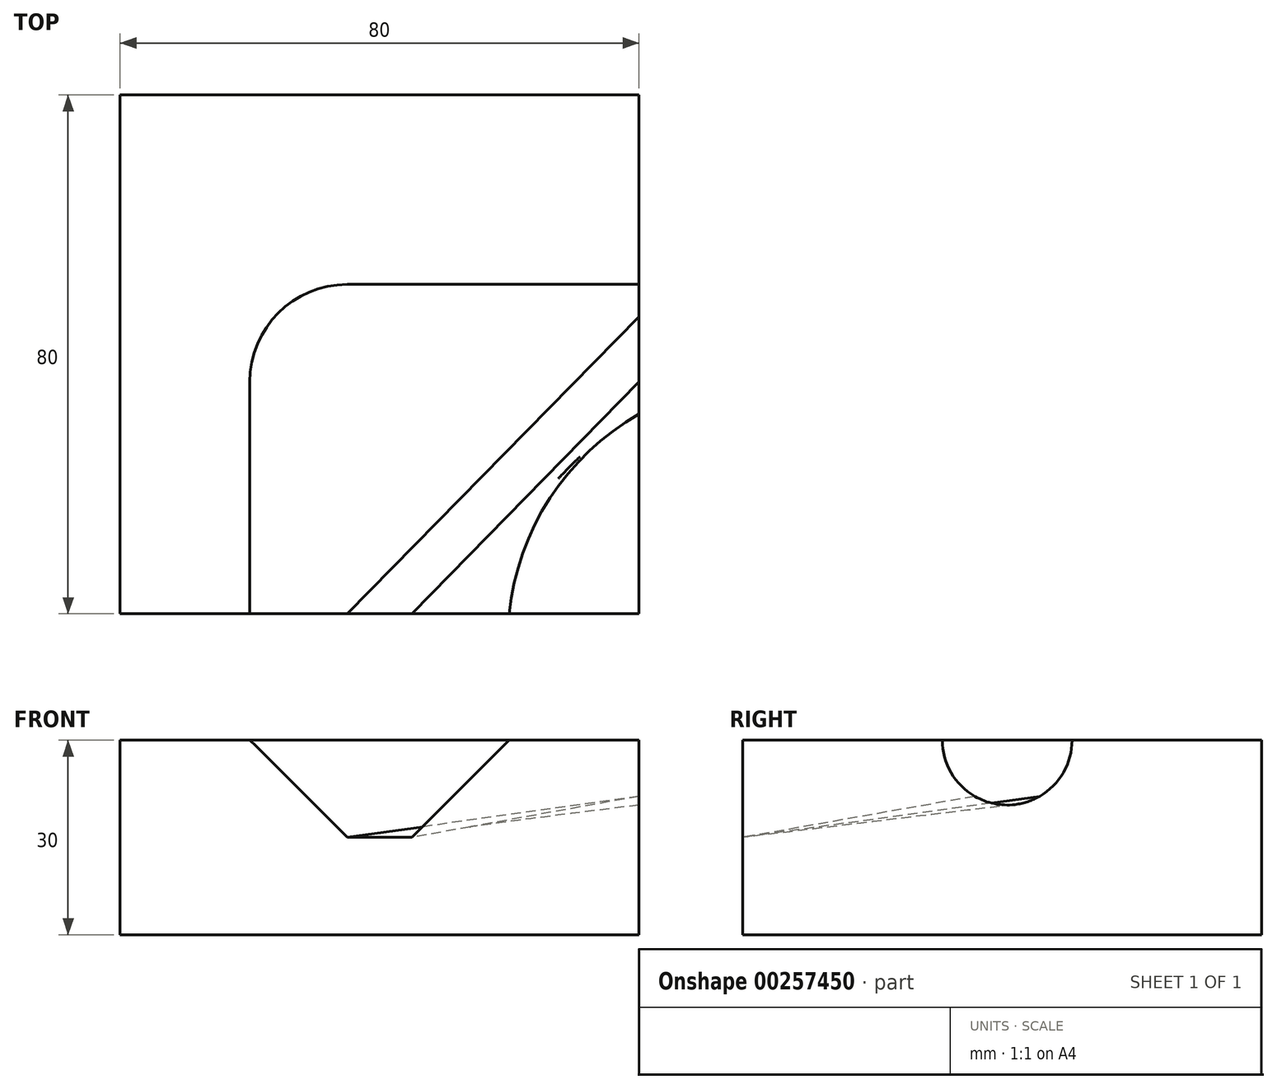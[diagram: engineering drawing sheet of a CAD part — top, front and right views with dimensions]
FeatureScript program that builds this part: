
annotation { "Feature Type Name" : "Feature", "Feature Type Description" : "" }
export const myFeature = defineFeature(function(context is Context, id is Id, definition is map)
    precondition{}
    {
        {
            var Q0;
            Q0=qCreatedBy(makeId("Top.planeOp"),FACE);
            var sketch = newSketch(context, id + "F0", { "sketchPlane" : qUnion([Q0])});
            skLineSegment(sketch, "E0.bottom", {"start": v(-80, 80) * mm, "end": v(0, 80) * mm});
            skLineSegment(sketch, "E0.top", {"start": v(-80, 0) * mm, "end": v(0, 0) * mm});
            skLineSegment(sketch, "E0.left", {"start": v(-80, 80) * mm, "end": v(-80, 0) * mm});
            skLineSegment(sketch, "E0.right", {"start": v(0, 80) * mm, "end": v(0, 0) * mm});
            skArc(sketch, "E1", {"start": v(-45, 50.78) * mm, "mid": v(-55.6, 46.38) * mm, "end": v(-60, 35.78) * mm});
            skArc(sketch, "E2", {"start": v(0, 30.78) * mm, "mid": v(-13.74, 17.82) * mm, "end": v(-20, 0) * mm});
            skLineSegment(sketch, "E3", {"start": v(-45, 50.78) * mm, "end": v(0, 50.78) * mm});
            skLineSegment(sketch, "E4", {"start": v(-60, 35.78) * mm, "end": v(-60, 0) * mm});
            skSolve(sketch);
        }
        {
            var Q0;
            {var subQ1=sQuery(id+"F0.wireOp",EDGE,"E0.bottom");Q0=makeQuery(id+"F0.imprint","IMPRINT",FACE,{"disambiguationData":[TD([[makeQuery(id+"F0.imprint","IMPRINT",EDGE,{"derivedFrom":subQ1}),-1.0]])]});}
            var Q1;
            Q1=makeQuery(id+"F0.imprint","IMPRINT",FACE,{"disambiguationData":[TD([[makeQuery(id+"F0.imprint","IMPRINT",EDGE,{"derivedFrom":sQuery(id+"F0.wireOp",EDGE,"E1")}),1.0]])]});
            var Q2;
            {var subQ3=sQuery(id+"F0.wireOp",EDGE,"E2");Q2=makeQuery(id+"F0.imprint","IMPRINT",FACE,{"disambiguationData":[TD([[makeQuery(id+"F0.imprint","IMPRINT",EDGE,{"derivedFrom":subQ3}),1.0]])]});}
            extrude(context, id + "F1", {"entities" : qUnion([Q0, Q1, Q2]), "oppositeDirection" : true, "depth" : 30 * mm});
        }
        {
            var Q0;
            Q0=makeQuery(id+"F1.opExtrude","SWEPT_FACE",FACE,{"disambiguationData":[OSD([sQuery(id+"F0.wireOp",EDGE,"E0.right")])]});
            cPlane(context, id + "F2", {"entities" : qUnion([Q0]), "cplaneType" : CPlaneType.OFFSET, "offset" : 0 * mm, "width" : 150 * mm, "height" : 150 * mm});
        }
        {
            var Q0;
            Q0=qCreatedBy(id+"F2.planeOp",FACE);
            var sketch = newSketch(context, id + "F3", { "sketchPlane" : qUnion([Q0])});
            skArc(sketch, "E5", {"start": v(30.78, 0) * mm, "mid": v(40.78, -10) * mm, "end": v(50.78, 0) * mm});
            skLineSegment(sketch, "E6.0", {"start": v(35.78, 0) * mm, "end": v(0, 0) * mm});
            skLineSegment(sketch, "E7.0", {"start": v(50.78, 0) * mm, "end": v(35.78, 0) * mm});
            skLineSegment(sketch, "E8.0", {"start": v(30.78, 0) * mm, "end": v(0, 0) * mm});
            skLineSegment(sketch, "E9.0", {"start": v(80, 0) * mm, "end": v(0, 0) * mm});
            skSolve(sketch);
        }
        {
            var Q0;
            Q0=makeQuery(id+"F1.opExtrude","SWEPT_FACE",FACE,{"disambiguationData":[OSD([sQuery(id+"F0.wireOp",EDGE,"E0.top")])]});
            cPlane(context, id + "F4", {"entities" : qUnion([Q0]), "cplaneType" : CPlaneType.OFFSET, "offset" : 0 * mm, "width" : 150 * mm, "height" : 150 * mm});
        }
        {
            var Q0;
            Q0=qCreatedBy(id+"F4.planeOp",FACE);
            var sketch = newSketch(context, id + "F5", { "sketchPlane" : qUnion([Q0])});
            skLineSegment(sketch, "E10.0", {"start": v(-80, 0) * mm, "end": v(0, 0) * mm});
            skLineSegment(sketch, "E11", {"start": v(-60, 0) * mm, "end": v(-45, -15) * mm});
            skLineSegment(sketch, "E12", {"start": v(-45, -15) * mm, "end": v(-35, -15) * mm});
            skLineSegment(sketch, "E13", {"start": v(-35, -15) * mm, "end": v(-20, 0) * mm});
            skSolve(sketch);
        }
        {
            var Q0;
            {var subQ1=sQuery(id+"F0.wireOp",EDGE,"E0.bottom");Q0=makeQuery(id+"F0.imprint","IMPRINT",FACE,{"disambiguationData":[TD([[makeQuery(id+"F0.imprint","IMPRINT",EDGE,{"derivedFrom":subQ1}),-1.0]])]});}
            var sketch = newSketch(context, id + "F6", { "sketchPlane" : qUnion([Q0])});
            skLineSegment(sketch, "E14.0", {"start": v(-45, 50.78) * mm, "end": v(0, 50.78) * mm});
            skArc(sketch, "E15.0", {"start": v(-45, 50.78) * mm, "mid": v(-55.6, 46.38) * mm, "end": v(-60, 35.78) * mm});
            skLineSegment(sketch, "E16.0", {"start": v(-60, 35.78) * mm, "end": v(-60, 0) * mm});
            skSolve(sketch);
        }
        {
            var Q1;
            {var subQ0=sQuery(id+"F3.wireOp",EDGE,"E5");Q1=makeQuery(id+"F3.imprint","IMPRINT",FACE,{"disambiguationData":[TD([[makeQuery(id+"F3.imprint","IMPRINT",EDGE,{"derivedFrom":subQ0}),1.0]])]});}
            var Q2;
            {var subQ0=sQuery(id+"F5.wireOp",EDGE,"E11");Q2=makeQuery(id+"F5.imprint","IMPRINT",FACE,{"disambiguationData":[TD([[makeQuery(id+"F5.imprint","IMPRINT",EDGE,{"derivedFrom":subQ0}),1.0]])]});}
            var Q3;
            Q3=sQuery(id+"F0.wireOp",EDGE,"E2");
            var Q4;
            Q4 = qConstructionFilter(qBodyType(qCreatedBy(id + "F6" ,EDGE), BodyType.WIRE), ConstructionObject.NO);
            loft(context, id + "F7", {"operationType" : NewBodyOperationType.REMOVE, "addGuides" : true, "sheetProfilesArray" : [{ "sheetProfileEntities" : qUnion([Q1]) }, { "sheetProfileEntities" : qUnion([Q2]) }], "guidesArray" : [{ "guideEntities" : qUnion([Q3]), "guideDerivativeType" : LoftGuideDerivativeType.DEFAULT, "guideDerivativeMagnitude" : 1 }, { "guideEntities" : qUnion([Q4]), "guideDerivativeType" : LoftGuideDerivativeType.DEFAULT, "guideDerivativeMagnitude" : 1 }]});
        }
    });
